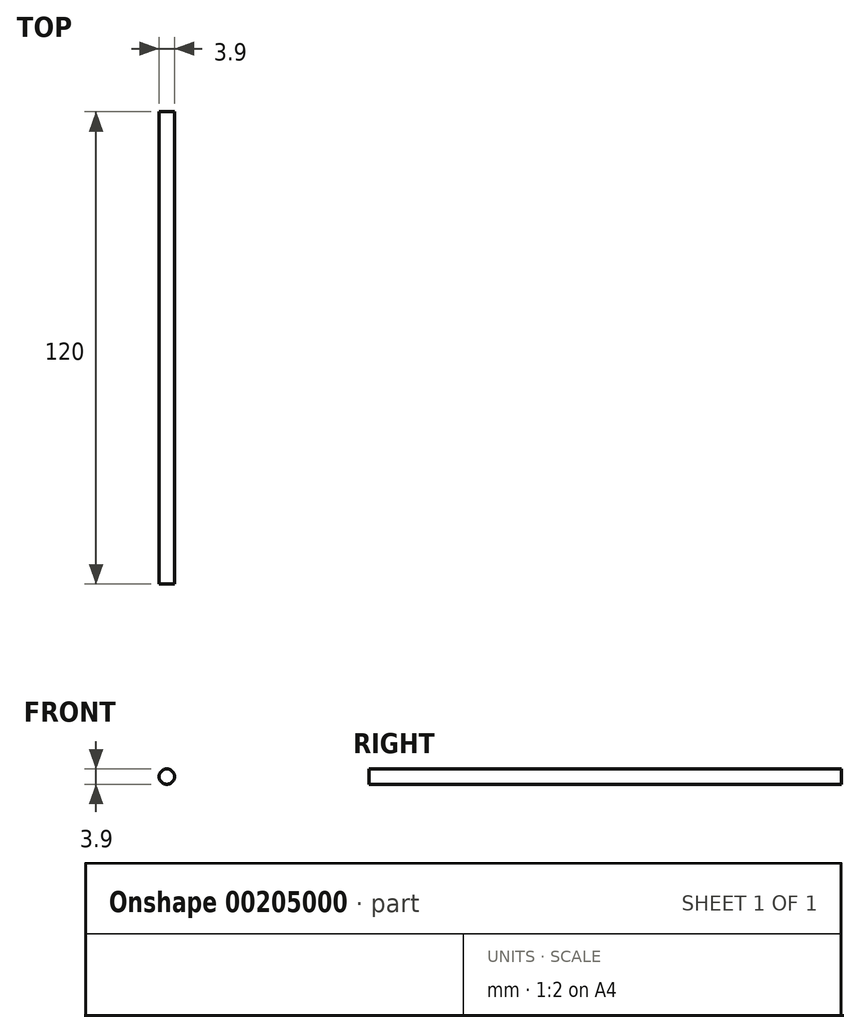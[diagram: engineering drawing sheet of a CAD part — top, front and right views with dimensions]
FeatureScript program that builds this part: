
annotation { "Feature Type Name" : "Feature", "Feature Type Description" : "" }
export const myFeature = defineFeature(function(context is Context, id is Id, definition is map)
    precondition{}
    {
        {
            var Q0;
            Q0=qCreatedBy(makeId("Front.planeOp"),FACE);
            var sketch = newSketch(context, id + "F0", { "sketchPlane" : qUnion([Q0])});
            skCircle(sketch, "E0", {"center": v(0, 0) * mm, "radius": 1.95 * mm});
            skSolve(sketch);
        }
        {
            var Q0;
            Q0 = qSketchRegion(id + "F0", true);
            extrude(context, id + "F1", {"entities" : qUnion([Q0]), "depth" : 120 * mm});
        }
    });
